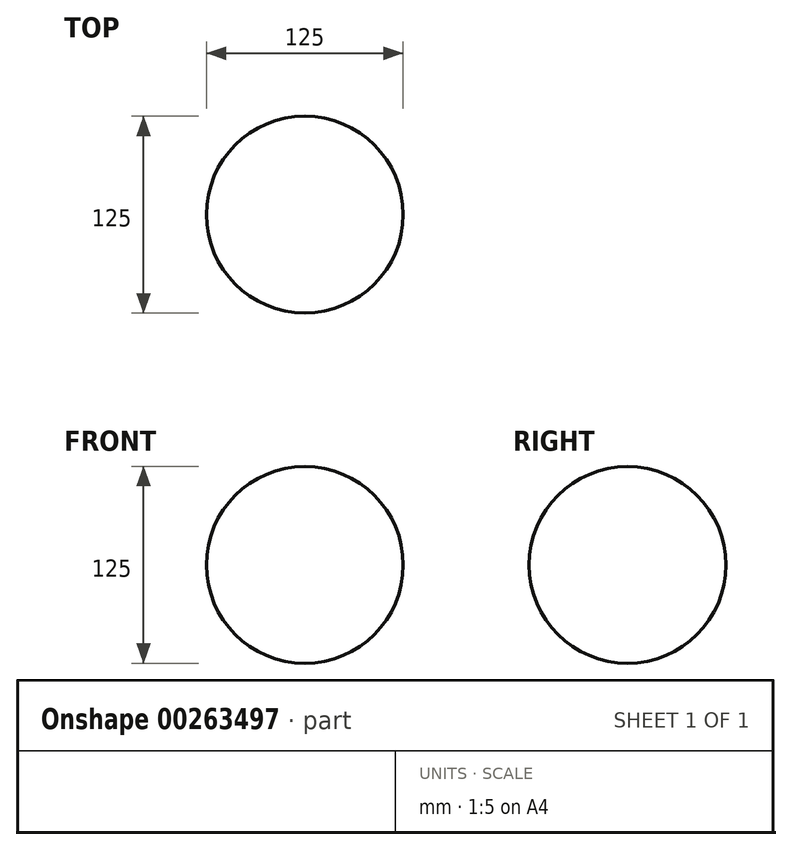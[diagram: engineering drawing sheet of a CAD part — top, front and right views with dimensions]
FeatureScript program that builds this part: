
annotation { "Feature Type Name" : "Feature", "Feature Type Description" : "" }
export const myFeature = defineFeature(function(context is Context, id is Id, definition is map)
    precondition{}
    {
        {
            var Q0;
            Q0=qCreatedBy(makeId("Front.planeOp"),FACE);
            var sketch = newSketch(context, id + "F0", { "sketchPlane" : qUnion([Q0])});
            skLineSegment(sketch, "E0", {"start": v(0, 76.05) * mm, "end": v(0, -76.33) * mm, "construction": true});
            skArc(sketch, "E1", {"start": v(0, 62.5) * mm, "mid": v(-62.5, 0) * mm, "end": v(0, -62.5) * mm});
            skSolve(sketch);
        }
        {
            var Q0;
            Q0=sQuery(id+"F0.wireOp",EDGE,"E0");
            var Q1;
            Q1=sQuery(id+"F0.wireOp",EDGE,"E1");
            var Q2;
            Q2=sQuery(id+"F0.wireOp",EDGE,"E0");
            revolve(context, id + "F1", {"bodyType" : ToolBodyType.SURFACE, "surfaceEntities" : qUnion([Q0, Q1]), "axis" : qUnion([Q2]), "revolveType" : RevolveType.FULL});
        }
    });
